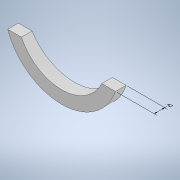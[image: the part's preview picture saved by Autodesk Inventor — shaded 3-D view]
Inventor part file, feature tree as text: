
AUTODESK INVENTOR PART (.ipt)
format: ipt  version: 2020.3 (Build 243373000, 373)  size: 110,592 bytes
history: native  units: in
note: dims shown in document units (in); Inventor stores cm internally (conversion verified against a paired STEP export)
features: other x2, plane x2, sketch x1, extrude x1
ambient origin geometry x8: Origin, YZ Plane, XZ Plane, XY Plane, X Axis, Y Axis, Z Axis, Center Point
bodies: Solid1 (feature_tree)
feature tree (6):
  other  "Annotations"
  sketch  "Sketch1"  dims[d6=1.0in d7=0.0in d10=0.417in d8=0.0in d9=0.3937in]
  plane  "Work Plane3"
  extrude  "Extrusion1"  Depth=0.3937in TaperAngle=0.0deg
  plane  "Work Plane2"
  other  "Linear Dimension 1"
